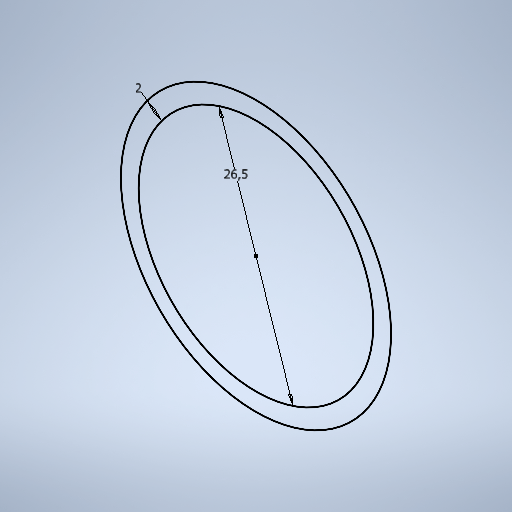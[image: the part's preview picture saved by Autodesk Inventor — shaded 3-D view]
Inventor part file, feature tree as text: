
AUTODESK INVENTOR PART (.ipt)
format: ipt  version: 2025 (Build 290162010, 162A)  size: 254,464 bytes
history: native  units: mm
features: sketch x1
ambient origin geometry x8: Origin, YZ Plane, XZ Plane, XY Plane, X Axis, Y Axis, Z Axis, Center Point
feature tree (1):
  sketch  "Sketch1"  dims[d0=2.0mm d1=26.5mm]
